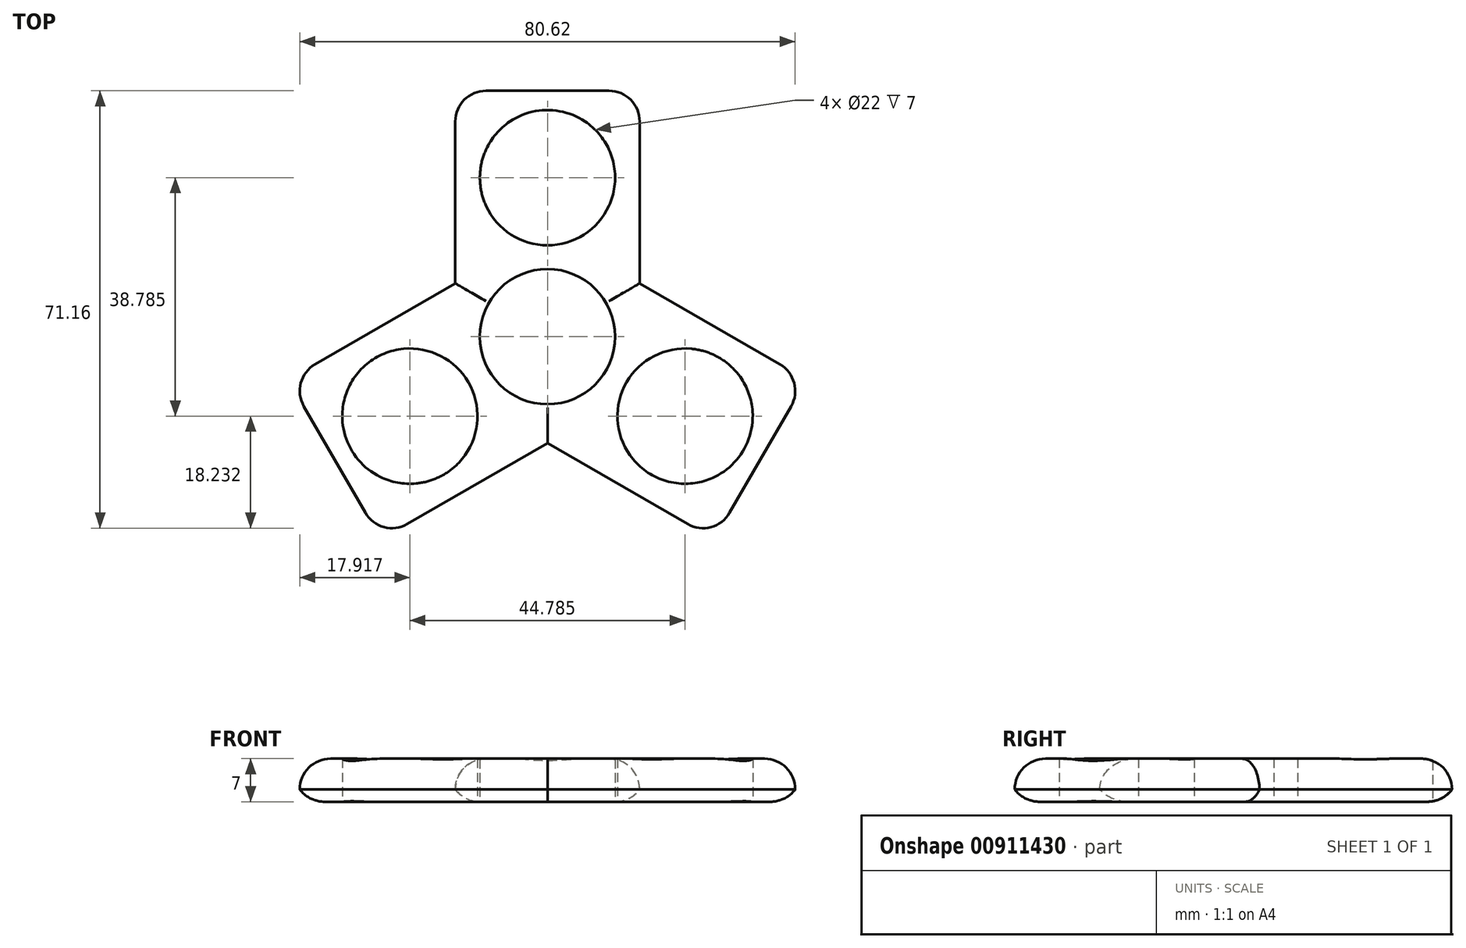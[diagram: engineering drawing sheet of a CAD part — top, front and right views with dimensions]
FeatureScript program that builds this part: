
annotation { "Feature Type Name" : "Feature", "Feature Type Description" : "" }
export const myFeature = defineFeature(function(context is Context, id is Id, definition is map)
    precondition{}
    {
        {
            var Q0;
            Q0=qCreatedBy(makeId("Top.planeOp"),FACE);
            var sketch = newSketch(context, id + "F0", { "sketchPlane" : qUnion([Q0])});
            skCircle(sketch, "E0", {"center": v(0, 0) * mm, "radius": 11 * mm});
            skLineSegment(sketch, "E1.bottom", {"start": v(0, 0) * mm, "end": v(15, 0) * mm});
            skLineSegment(sketch, "E1.top", {"start": v(0, 40) * mm, "end": v(15, 40) * mm});
            skLineSegment(sketch, "E1.left", {"start": v(0, 0) * mm, "end": v(0, 40) * mm});
            skLineSegment(sketch, "E1.right", {"start": v(15, 0) * mm, "end": v(15, 40) * mm});
            skLineSegment(sketch, "E2.bottom", {"start": v(0, 0) * mm, "end": v(-15, 0) * mm});
            skLineSegment(sketch, "E2.top", {"start": v(0, 40) * mm, "end": v(-15, 40) * mm});
            skLineSegment(sketch, "E2.right", {"start": v(-15, 0) * mm, "end": v(-15, 40) * mm});
            skLineSegment(sketch, "E3", {"start": v(0, 0) * mm, "end": v(0, 14.06) * mm});
            skLineSegment(sketch, "E4", {"start": v(0, 40) * mm, "end": v(0, 25.86) * mm});
            skCircle(sketch, "E5", {"center": v(0, 25.86) * mm, "radius": 11 * mm});
            skSolve(sketch);
        }
        {
            var Q0;
            {var subQ5=sQuery(id+"F0.wireOp",EDGE,"E1.top");Q0=makeQuery(id+"F0.imprint","IMPRINT",FACE,{"disambiguationData":[TD([[makeQuery(id+"F0.imprint","IMPRINT",EDGE,{"derivedFrom":subQ5}),-1.0]])]});}
            var Q1;
            {var subQ5=sQuery(id+"F0.wireOp",EDGE,"E2.top");Q1=makeQuery(id+"F0.imprint","IMPRINT",FACE,{"disambiguationData":[TD([[makeQuery(id+"F0.imprint","IMPRINT",EDGE,{"derivedFrom":subQ5}),1.0]])]});}
            extrude(context, id + "F1", {"entities" : qUnion([Q0, Q1]), "depth" : 7 * mm, "offsetDistance" : 25 * mm});
        }
        {
            var Q0;
            Q0=qCreatedBy(makeId("Front.planeOp"),FACE);
            var sketch = newSketch(context, id + "F2", { "sketchPlane" : qUnion([Q0])});
            skLineSegment(sketch, "E6", {"start": v(0, 0) * mm, "end": v(0, 39.1) * mm});
            skSolve(sketch);
        }
        {
            var Q0;
            Q0=makeQuery(id+"F1.opExtrude","SWEPT_BODY",BODY,{"disambiguationData":[OSD([sQuery(id+"F0.wireOp",EDGE,"E0"),sQuery(id+"F0.wireOp",EDGE,"E1.bottom"),sQuery(id+"F0.wireOp",EDGE,"E1.top"),sQuery(id+"F0.wireOp",EDGE,"E1.right"),sQuery(id+"F0.wireOp",EDGE,"E2.bottom"),sQuery(id+"F0.wireOp",EDGE,"E2.top"),sQuery(id+"F0.wireOp",EDGE,"E2.right"),sQuery(id+"F0.wireOp",EDGE,"E5")])]});
            var Q1;
            Q1=sQuery(id+"F2.wireOp",EDGE,"E6");
            transform(context, id + "F3", {"entities" : qUnion([Q0]), "transformType" : TransformType.ROTATION, "transformAxis" : qUnion([Q1]), "angle" : 120 * degree, "makeCopy" : true});
        }
        {
            var Q0;
            Q0=makeQuery(id+"F3.opPattern","COPY",BODY,{"derivedFrom":makeQuery(id+"F1.opExtrude","SWEPT_BODY",BODY,{"disambiguationData":[OSD([sQuery(id+"F0.wireOp",EDGE,"E0"),sQuery(id+"F0.wireOp",EDGE,"E1.bottom"),sQuery(id+"F0.wireOp",EDGE,"E1.top"),sQuery(id+"F0.wireOp",EDGE,"E1.right"),sQuery(id+"F0.wireOp",EDGE,"E2.bottom"),sQuery(id+"F0.wireOp",EDGE,"E2.top"),sQuery(id+"F0.wireOp",EDGE,"E2.right"),sQuery(id+"F0.wireOp",EDGE,"E5")])]}),"instanceName":"1"});
            var Q1;
            Q1=sQuery(id+"F2.wireOp",EDGE,"E6");
            transform(context, id + "F4", {"entities" : qUnion([Q0]), "transformType" : TransformType.ROTATION, "transformAxis" : qUnion([Q1]), "angle" : 240 * degree, "oppositeDirection" : true, "makeCopy" : true});
        }
        {
            var Q0;
            Q0=makeQuery(id+"F3.opPattern","COPY",BODY,{"derivedFrom":makeQuery(id+"F1.opExtrude","SWEPT_BODY",BODY,{"disambiguationData":[OSD([sQuery(id+"F0.wireOp",EDGE,"E0"),sQuery(id+"F0.wireOp",EDGE,"E1.bottom"),sQuery(id+"F0.wireOp",EDGE,"E1.top"),sQuery(id+"F0.wireOp",EDGE,"E1.right"),sQuery(id+"F0.wireOp",EDGE,"E2.bottom"),sQuery(id+"F0.wireOp",EDGE,"E2.top"),sQuery(id+"F0.wireOp",EDGE,"E2.right"),sQuery(id+"F0.wireOp",EDGE,"E5")])]}),"instanceName":"1"});
            var Q1;
            Q1=makeQuery(id+"F4.opPattern","COPY",BODY,{"derivedFrom":makeQuery(id+"F3.opPattern","COPY",BODY,{"derivedFrom":makeQuery(id+"F1.opExtrude","SWEPT_BODY",BODY,{"disambiguationData":[OSD([sQuery(id+"F0.wireOp",EDGE,"E0"),sQuery(id+"F0.wireOp",EDGE,"E1.bottom"),sQuery(id+"F0.wireOp",EDGE,"E1.top"),sQuery(id+"F0.wireOp",EDGE,"E1.right"),sQuery(id+"F0.wireOp",EDGE,"E2.bottom"),sQuery(id+"F0.wireOp",EDGE,"E2.top"),sQuery(id+"F0.wireOp",EDGE,"E2.right"),sQuery(id+"F0.wireOp",EDGE,"E5")])]}),"instanceName":"1"}),"instanceName":"1"});
            var Q2;
            Q2=makeQuery(id+"F1.opExtrude","SWEPT_BODY",BODY,{"disambiguationData":[OSD([sQuery(id+"F0.wireOp",EDGE,"E0"),sQuery(id+"F0.wireOp",EDGE,"E1.bottom"),sQuery(id+"F0.wireOp",EDGE,"E1.top"),sQuery(id+"F0.wireOp",EDGE,"E1.right"),sQuery(id+"F0.wireOp",EDGE,"E2.bottom"),sQuery(id+"F0.wireOp",EDGE,"E2.top"),sQuery(id+"F0.wireOp",EDGE,"E2.right"),sQuery(id+"F0.wireOp",EDGE,"E5")])]});
            booleanBodies(context, id + "F5", {"operationType" : BooleanOperationType.UNION, "tools" : qUnion([Q0, Q1, Q2])});
        }
        {
            var Q0;
            Q0=makeQuery(id+"F1.opExtrude","CAP_EDGE",EDGE,{"disambiguationData":[OSD([sQuery(id+"F0.wireOp",EDGE,"E1.right")])],"isStart":false});
            var Q1;
            Q1=makeQuery(id+"F1.opExtrude","CAP_EDGE",EDGE,{"disambiguationData":[OSD([sQuery(id+"F0.wireOp",EDGE,"E1.top"),sQuery(id+"F0.wireOp",EDGE,"E2.top")])],"isStart":false});
            fillet(context, id + "F6", {"entities" : qUnion([Q0, Q1]), "radius" : 5 * mm, "tangentPropagation" : true, "allowEdgeOverflow" : false});
        }
        {
            var Q0;
            Q0=makeQuery(id+"F3.opPattern","COPY",EDGE,{"derivedFrom":makeQuery(id+"F1.opExtrude","CAP_EDGE",EDGE,{"disambiguationData":[OSD([sQuery(id+"F0.wireOp",EDGE,"E2.right")])],"isStart":false}),"instanceName":"1"});
            var Q1;
            Q1=makeQuery(id+"F3.opPattern","COPY",EDGE,{"derivedFrom":makeQuery(id+"F1.opExtrude","CAP_EDGE",EDGE,{"disambiguationData":[OSD([sQuery(id+"F0.wireOp",EDGE,"E1.top"),sQuery(id+"F0.wireOp",EDGE,"E2.top")])],"isStart":false}),"instanceName":"1"});
            fillet(context, id + "F7", {"entities" : qUnion([Q0, Q1]), "radius" : 5 * mm, "tangentPropagation" : true, "allowEdgeOverflow" : false});
        }
        {
            var Q0;
            Q0=makeQuery(id+"F4.opPattern","COPY",EDGE,{"derivedFrom":makeQuery(id+"F3.opPattern","COPY",EDGE,{"derivedFrom":makeQuery(id+"F1.opExtrude","CAP_EDGE",EDGE,{"disambiguationData":[OSD([sQuery(id+"F0.wireOp",EDGE,"E1.right")])],"isStart":false}),"instanceName":"1"}),"instanceName":"1"});
            var Q1;
            Q1=makeQuery(id+"F4.opPattern","COPY",EDGE,{"derivedFrom":makeQuery(id+"F3.opPattern","COPY",EDGE,{"derivedFrom":makeQuery(id+"F1.opExtrude","CAP_EDGE",EDGE,{"disambiguationData":[OSD([sQuery(id+"F0.wireOp",EDGE,"E1.top"),sQuery(id+"F0.wireOp",EDGE,"E2.top")])],"isStart":false}),"instanceName":"1"}),"instanceName":"1"});
            fillet(context, id + "F8", {"entities" : qUnion([Q0, Q1]), "radius" : 5 * mm, "tangentPropagation" : true, "allowEdgeOverflow" : false});
        }
        {
            var Q0;
            Q0=makeQuery(id+"F1.opExtrude","CAP_EDGE",EDGE,{"disambiguationData":[OSD([sQuery(id+"F0.wireOp",EDGE,"E2.right")])],"isStart":false});
            var Q1;
            Q1=makeQuery(id+"F3.opPattern","COPY",EDGE,{"derivedFrom":makeQuery(id+"F1.opExtrude","CAP_EDGE",EDGE,{"disambiguationData":[OSD([sQuery(id+"F0.wireOp",EDGE,"E1.right")])],"isStart":false}),"instanceName":"1"});
            var Q2;
            Q2=makeQuery(id+"F4.opPattern","COPY",EDGE,{"derivedFrom":makeQuery(id+"F3.opPattern","COPY",EDGE,{"derivedFrom":makeQuery(id+"F1.opExtrude","CAP_EDGE",EDGE,{"disambiguationData":[OSD([sQuery(id+"F0.wireOp",EDGE,"E2.right")])],"isStart":false}),"instanceName":"1"}),"instanceName":"1"});
            fillet(context, id + "F9", {"entities" : qUnion([Q0, Q1, Q2]), "radius" : 5 * mm, "tangentPropagation" : true, "allowEdgeOverflow" : false});
        }
        {
            var Q0;
            Q0=makeQuery(id+"F7.opFillet","BLEND_EDGE",EDGE,{"blendedFrom":[makeQuery(id+"F3.opPattern","COPY",EDGE,{"derivedFrom":makeQuery(id+"F1.opExtrude","CAP_EDGE",EDGE,{"disambiguationData":[OSD([sQuery(id+"F0.wireOp",EDGE,"E1.top"),sQuery(id+"F0.wireOp",EDGE,"E2.top")])],"isStart":false}),"instanceName":"1"}),makeQuery(id+"F3.opPattern","COPY",EDGE,{"derivedFrom":makeQuery(id+"F1.opExtrude","CAP_EDGE",EDGE,{"disambiguationData":[OSD([sQuery(id+"F0.wireOp",EDGE,"E2.right")])],"isStart":false}),"instanceName":"1"})],"blendedInto":[]});
            var Q1;
            Q1=makeQuery(id+"F8.opFillet","BLEND_EDGE",EDGE,{"blendedFrom":[makeQuery(id+"F4.opPattern","COPY",EDGE,{"derivedFrom":makeQuery(id+"F3.opPattern","COPY",EDGE,{"derivedFrom":makeQuery(id+"F1.opExtrude","CAP_EDGE",EDGE,{"disambiguationData":[OSD([sQuery(id+"F0.wireOp",EDGE,"E1.top"),sQuery(id+"F0.wireOp",EDGE,"E2.top")])],"isStart":false}),"instanceName":"1"}),"instanceName":"1"}),makeQuery(id+"F4.opPattern","COPY",EDGE,{"derivedFrom":makeQuery(id+"F3.opPattern","COPY",EDGE,{"derivedFrom":makeQuery(id+"F1.opExtrude","CAP_EDGE",EDGE,{"disambiguationData":[OSD([sQuery(id+"F0.wireOp",EDGE,"E1.right")])],"isStart":false}),"instanceName":"1"}),"instanceName":"1"})],"blendedInto":[]});
            var Q2;
            Q2=makeQuery(id+"F6.opFillet","BLEND_EDGE",EDGE,{"blendedFrom":[makeQuery(id+"F1.opExtrude","CAP_EDGE",EDGE,{"disambiguationData":[OSD([sQuery(id+"F0.wireOp",EDGE,"E1.top"),sQuery(id+"F0.wireOp",EDGE,"E2.top")])],"isStart":false}),makeQuery(id+"F1.opExtrude","CAP_EDGE",EDGE,{"disambiguationData":[OSD([sQuery(id+"F0.wireOp",EDGE,"E1.right")])],"isStart":false})],"blendedInto":[]});
            fillet(context, id + "F10", {"entities" : qUnion([Q0, Q1, Q2]), "radius" : 5 * mm, "tangentPropagation" : true, "allowEdgeOverflow" : false});
        }
        {
            var Q0;
            {var subQ0=sQuery(id+"F0.wireOp",EDGE,"E2.right");var subQ1=sQuery(id+"F0.wireOp",EDGE,"E2.top");var subQ2=makeQuery(id+"F1.opExtrude","CAP_FACE",FACE,{"disambiguationData":[OSD([sQuery(id+"F0.wireOp",EDGE,"E0"),sQuery(id+"F0.wireOp",EDGE,"E1.bottom"),sQuery(id+"F0.wireOp",EDGE,"E1.top"),sQuery(id+"F0.wireOp",EDGE,"E1.right"),sQuery(id+"F0.wireOp",EDGE,"E2.bottom"),subQ1,subQ0,sQuery(id+"F0.wireOp",EDGE,"E5")])],"isStart":true});var subQ3=makeQuery(id+"F3.opPattern","COPY",FACE,{"derivedFrom":subQ2,"instanceName":"1"});Q0=makeQuery(id+"F9.opFillet","BLEND_EDGE",EDGE,{"blendedFrom":[makeQuery(id+"F1.opExtrude","SWEPT_EDGE",EDGE,{"disambiguationData":[OSD([subQ1,subQ0])]}),makeQuery(id+"F5.opBoolean","MERGE",FACE,{"derivedFrom":[subQ2,subQ3,makeQuery(id+"F4.opPattern","COPY",FACE,{"derivedFrom":subQ3,"instanceName":"1"})]})],"blendedInto":[makeQuery(id+"F5.opBoolean","MERGE",FACE,{"derivedFrom":[subQ2,subQ3,makeQuery(id+"F4.opPattern","COPY",FACE,{"derivedFrom":subQ3,"instanceName":"1"})]})]});}
            var Q1;
            {var subQ0=sQuery(id+"F0.wireOp",EDGE,"E2.right");var subQ1=sQuery(id+"F0.wireOp",EDGE,"E2.top");var subQ2=makeQuery(id+"F1.opExtrude","CAP_FACE",FACE,{"disambiguationData":[OSD([sQuery(id+"F0.wireOp",EDGE,"E0"),sQuery(id+"F0.wireOp",EDGE,"E1.bottom"),sQuery(id+"F0.wireOp",EDGE,"E1.top"),sQuery(id+"F0.wireOp",EDGE,"E1.right"),sQuery(id+"F0.wireOp",EDGE,"E2.bottom"),subQ1,subQ0,sQuery(id+"F0.wireOp",EDGE,"E5")])],"isStart":true});var subQ3=makeQuery(id+"F3.opPattern","COPY",FACE,{"derivedFrom":subQ2,"instanceName":"1"});Q1=makeQuery(id+"F9.opFillet","BLEND_EDGE",EDGE,{"blendedFrom":[makeQuery(id+"F4.opPattern","COPY",EDGE,{"derivedFrom":makeQuery(id+"F3.opPattern","COPY",EDGE,{"derivedFrom":makeQuery(id+"F1.opExtrude","SWEPT_EDGE",EDGE,{"disambiguationData":[OSD([subQ1,subQ0])]}),"instanceName":"1"}),"instanceName":"1"}),makeQuery(id+"F5.opBoolean","MERGE",FACE,{"derivedFrom":[subQ2,subQ3,makeQuery(id+"F4.opPattern","COPY",FACE,{"derivedFrom":subQ3,"instanceName":"1"})]})],"blendedInto":[makeQuery(id+"F5.opBoolean","MERGE",FACE,{"derivedFrom":[subQ2,subQ3,makeQuery(id+"F4.opPattern","COPY",FACE,{"derivedFrom":subQ3,"instanceName":"1"})]})]});}
            var Q2;
            {var subQ0=sQuery(id+"F0.wireOp",EDGE,"E2.right");var subQ1=sQuery(id+"F0.wireOp",EDGE,"E2.top");var subQ2=makeQuery(id+"F1.opExtrude","CAP_FACE",FACE,{"disambiguationData":[OSD([sQuery(id+"F0.wireOp",EDGE,"E0"),sQuery(id+"F0.wireOp",EDGE,"E1.bottom"),sQuery(id+"F0.wireOp",EDGE,"E1.top"),sQuery(id+"F0.wireOp",EDGE,"E1.right"),sQuery(id+"F0.wireOp",EDGE,"E2.bottom"),subQ1,subQ0,sQuery(id+"F0.wireOp",EDGE,"E5")])],"isStart":true});var subQ3=makeQuery(id+"F3.opPattern","COPY",FACE,{"derivedFrom":subQ2,"instanceName":"1"});Q2=makeQuery(id+"F10.opFillet","BLEND_EDGE",EDGE,{"blendedFrom":[makeQuery(id+"F3.opPattern","COPY",EDGE,{"derivedFrom":makeQuery(id+"F1.opExtrude","SWEPT_EDGE",EDGE,{"disambiguationData":[OSD([subQ1,subQ0])]}),"instanceName":"1"}),makeQuery(id+"F5.opBoolean","MERGE",FACE,{"derivedFrom":[subQ2,subQ3,makeQuery(id+"F4.opPattern","COPY",FACE,{"derivedFrom":subQ3,"instanceName":"1"})]})],"blendedInto":[makeQuery(id+"F5.opBoolean","MERGE",FACE,{"derivedFrom":[subQ2,subQ3,makeQuery(id+"F4.opPattern","COPY",FACE,{"derivedFrom":subQ3,"instanceName":"1"})]})]});}
            fillet(context, id + "F11", {"entities" : qUnion([Q0, Q1, Q2]), "radius" : 5 * mm, "tangentPropagation" : true, "allowEdgeOverflow" : false});
        }
    });
